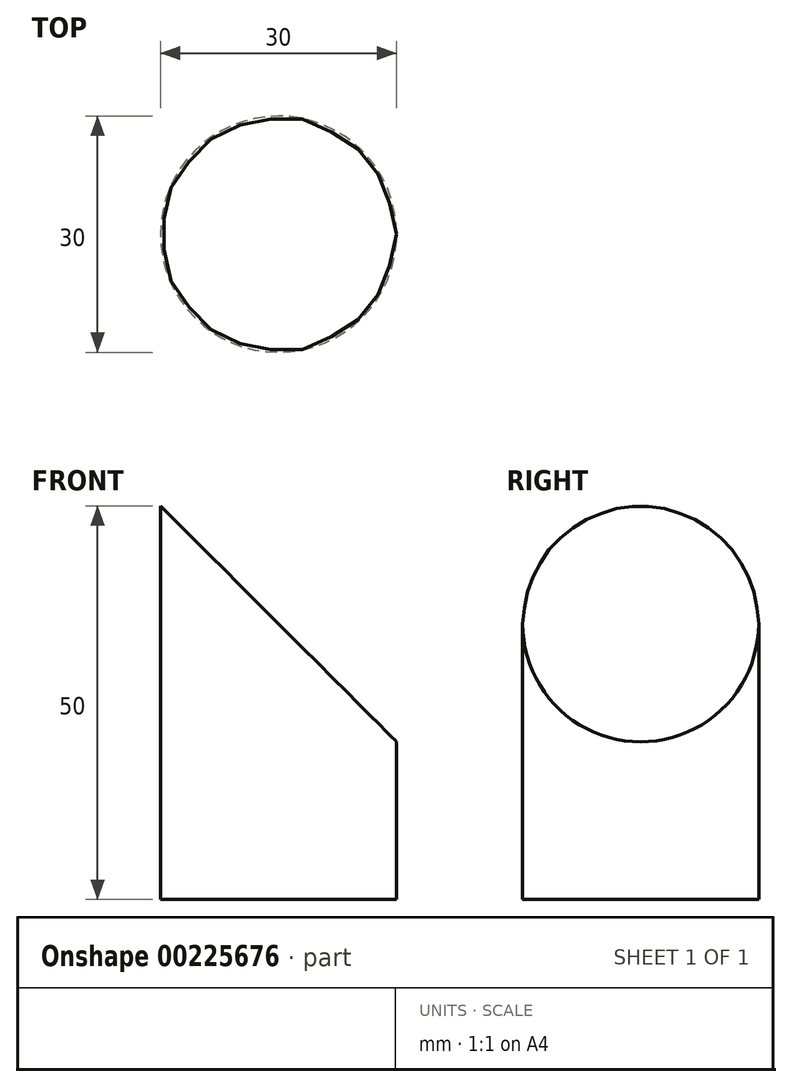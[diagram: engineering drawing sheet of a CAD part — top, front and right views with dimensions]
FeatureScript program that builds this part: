
annotation { "Feature Type Name" : "Feature", "Feature Type Description" : "" }
export const myFeature = defineFeature(function(context is Context, id is Id, definition is map)
    precondition{}
    {
        {
            var Q0;
            Q0=qCreatedBy(makeId("Top.planeOp"),FACE);
            var sketch = newSketch(context, id + "F0", { "sketchPlane" : qUnion([Q0])});
            skCircle(sketch, "E0", {"center": v(0, 0) * mm, "radius": 15 * mm});
            skSolve(sketch);
        }
        {
            var Q0;
            Q0=makeQuery(id+"F0.imprint","IMPRINT",FACE,{"disambiguationData":[TD([[makeQuery(id+"F0.imprint","IMPRINT",EDGE,{"derivedFrom":sQuery(id+"F0.wireOp",EDGE,"E0")}),1.0]])]});
            extrude(context, id + "F1", {"entities" : qUnion([Q0]), "depth" : 50 * mm});
        }
        {
            var Q0;
            Q0=qCreatedBy(makeId("Front.planeOp"),FACE);
            var sketch = newSketch(context, id + "F2", { "sketchPlane" : qUnion([Q0])});
            skLineSegment(sketch, "E1", {"start": v(-15, 0) * mm, "end": v(-15, 50) * mm});
            skLineSegment(sketch, "E2", {"start": v(-15, 0) * mm, "end": v(15, 0) * mm});
            skLineSegment(sketch, "E3", {"start": v(15, 0) * mm, "end": v(15, 20) * mm});
            skLineSegment(sketch, "E4", {"start": v(15, 20) * mm, "end": v(-15, 50) * mm});
            skLineSegment(sketch, "E5", {"start": v(15, 50) * mm, "end": v(15, 0) * mm, "construction": true});
            skLineSegment(sketch, "E6", {"start": v(-15, 0) * mm, "end": v(-15, 50) * mm, "construction": true});
            skSolve(sketch);
        }
        {
            var Q0;
            Q0=makeQuery(id+"F2.imprint","IMPRINT",FACE,{"disambiguationData":[TD([[makeQuery(id+"F2.imprint","IMPRINT",EDGE,{"derivedFrom":sQuery(id+"F2.wireOp",EDGE,"E1")}),-1.0]])]});
            extrude(context, id + "F3", {"entities" : qUnion([Q0]), "operationType" : NewBodyOperationType.INTERSECT, "endBound" : BoundingType.SYMMETRIC, "oppositeDirection" : true, "depth" : 50 * mm});
        }
    });
